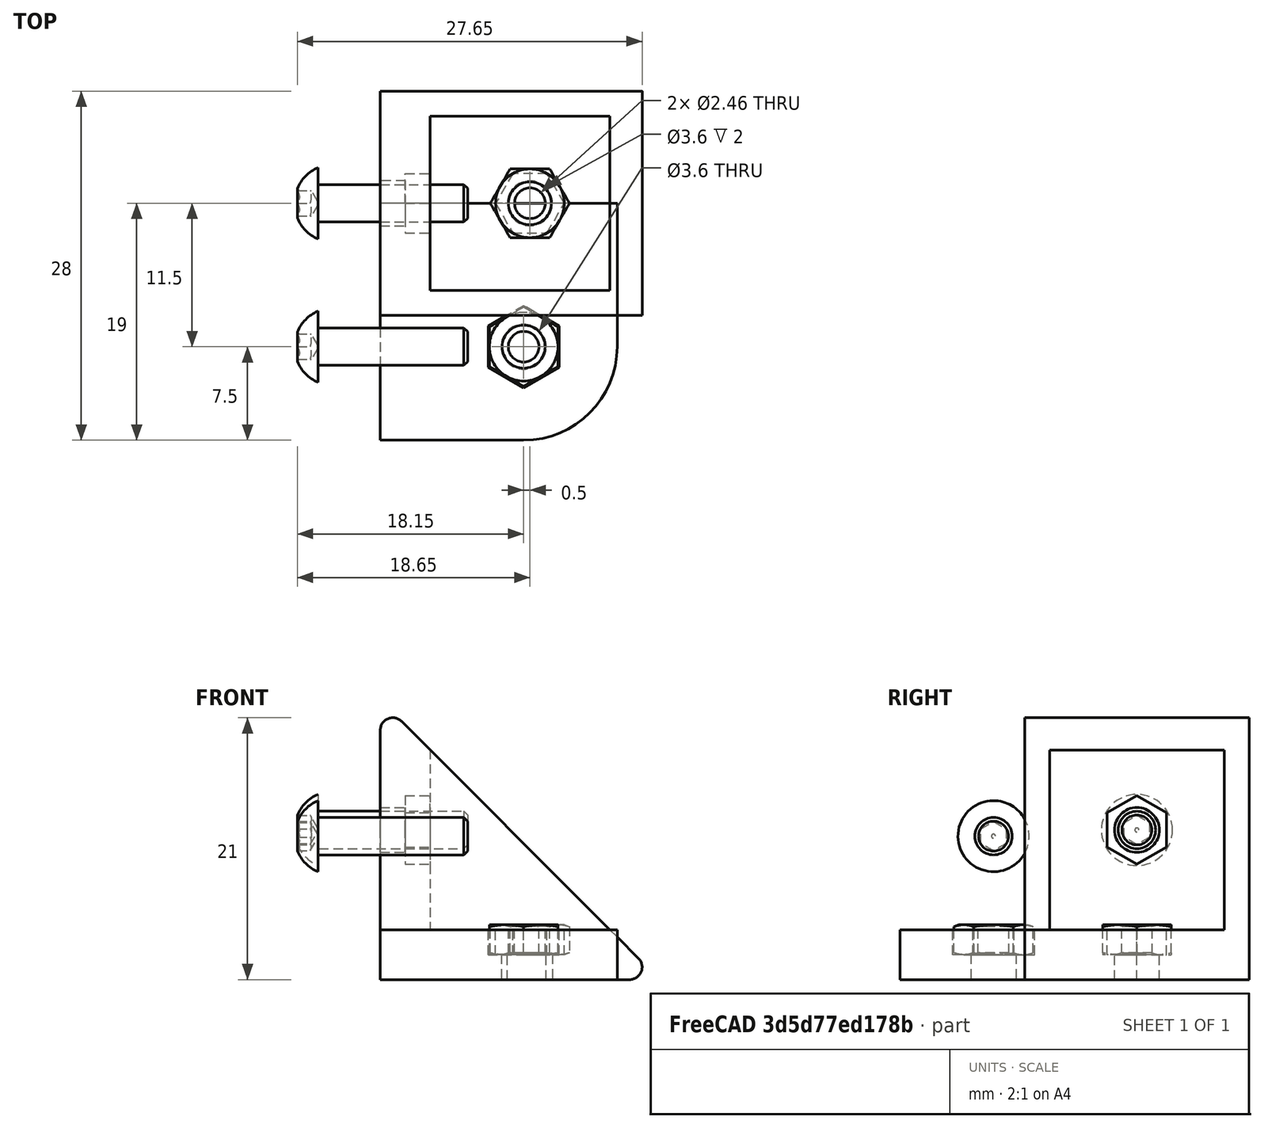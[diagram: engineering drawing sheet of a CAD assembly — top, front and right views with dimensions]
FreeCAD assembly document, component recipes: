
FREECAD ASSEMBLY — COMPONENT RECIPES ("Bracket")

This assembly document has 2 components, labeled P0..P1 below (a component is one placed body or linked part). 0 of them carry a construction recipe — the FreeCAD feature program that regenerates the part from scratch, quoted from this document or its linked companion documents; the rest are supplied as boundary geometry only. No exploded tour is included for this assembly.
COMPONENT P0 — geometry summary ("Corner_bracket"; no construction recipe available for this part):
  bounding box: 25.7 x 25.7 x 25.7 mm
  tessellated surface: 32,616 triangles
  volume: 4429 mm^3 (26% of its bounding box)
COMPONENT P1 — geometry summary ("Right_angle_bracket"; no construction recipe available for this part):
  bounding box: 27.7 x 27.7 x 18.0 mm
  tessellated surface: 21,852 triangles
  volume: 3218 mm^3 (23% of its bounding box)
  symmetry: mirror-symmetric across its y mid-plane
PROVENANCE & LICENSES
A FreeCAD (.FCStd) document from a public repository crawl; recipes are the document's own serialized feature recipes (and, for linked parts, companion documents' recipes).
License: as declared in the source repository (recorded in the dataset sidecar).
